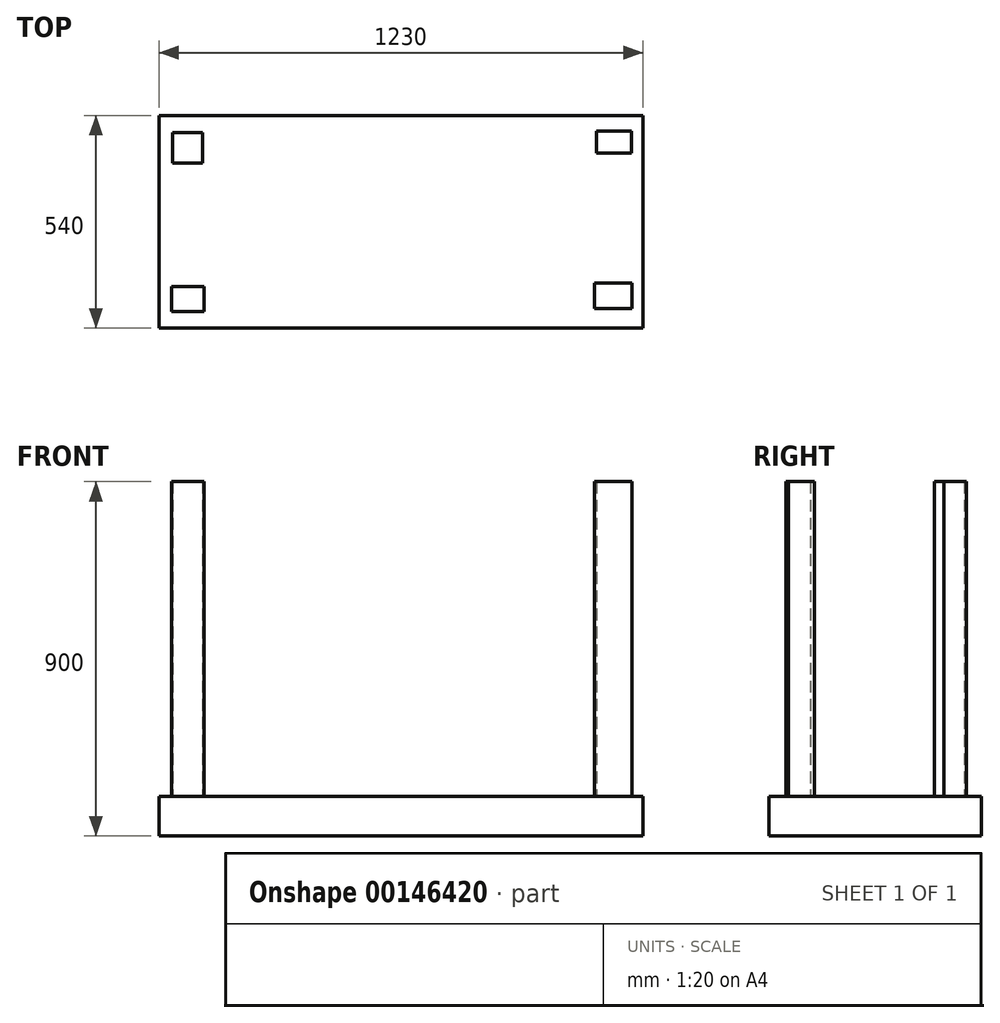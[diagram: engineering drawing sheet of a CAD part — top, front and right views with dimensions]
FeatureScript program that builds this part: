
annotation { "Feature Type Name" : "Feature", "Feature Type Description" : "" }
export const myFeature = defineFeature(function(context is Context, id is Id, definition is map)
    precondition{}
    {
        {
            var Q0;
            Q0=qCreatedBy(makeId("Top.planeOp"),FACE);
            var sketch = newSketch(context, id + "F0", { "sketchPlane" : qUnion([Q0])});
            skLineSegment(sketch, "E0.bottom", {"start": v(615, -270) * mm, "end": v(-615, -270) * mm});
            skLineSegment(sketch, "E0.top", {"start": v(615, 270) * mm, "end": v(-615, 270) * mm});
            skLineSegment(sketch, "E0.left", {"start": v(615, -270) * mm, "end": v(615, 270) * mm});
            skLineSegment(sketch, "E0.right", {"start": v(-615, -270) * mm, "end": v(-615, 270) * mm});
            skPoint(sketch, "E0.middle", {"position": v(0, 0) * mm});
            skSolve(sketch);
        }
        {
            var Q0;
            Q0 = qSketchRegion(id + "F0", true);
            extrude(context, id + "F1", {"entities" : qUnion([Q0]), "depth" : 100 * mm});
        }
        {
            var Q0;
            Q0=makeQuery(id+"F1.opExtrude","CAP_FACE",FACE,{"disambiguationData":[OSD([sQuery(id+"F0.wireOp",EDGE,"E0.bottom"),sQuery(id+"F0.wireOp",EDGE,"E0.top"),sQuery(id+"F0.wireOp",EDGE,"E0.left"),sQuery(id+"F0.wireOp",EDGE,"E0.right")])],"isStart":false});
            var sketch = newSketch(context, id + "F2", { "sketchPlane" : qUnion([Q0])});
            skLineSegment(sketch, "E1.bottom", {"start": v(-582.57, -227.2) * mm, "end": v(-500.5, -227.2) * mm});
            skLineSegment(sketch, "E1.top", {"start": v(-582.57, -164.73) * mm, "end": v(-500.5, -164.73) * mm});
            skLineSegment(sketch, "E1.left", {"start": v(-582.57, -227.2) * mm, "end": v(-582.57, -164.73) * mm});
            skLineSegment(sketch, "E1.right", {"start": v(-500.5, -227.2) * mm, "end": v(-500.5, -164.73) * mm});
            skLineSegment(sketch, "E2.bottom", {"start": v(-580.54, 226.4) * mm, "end": v(-503.8, 226.4) * mm});
            skLineSegment(sketch, "E2.top", {"start": v(-580.54, 150.06) * mm, "end": v(-503.8, 150.06) * mm});
            skLineSegment(sketch, "E2.left", {"start": v(-580.54, 226.4) * mm, "end": v(-580.54, 150.06) * mm});
            skLineSegment(sketch, "E2.right", {"start": v(-503.8, 226.4) * mm, "end": v(-503.8, 150.06) * mm});
            skLineSegment(sketch, "E3.bottom", {"start": v(585.54, 231.05) * mm, "end": v(497.23, 231.05) * mm});
            skLineSegment(sketch, "E3.top", {"start": v(585.54, 175.04) * mm, "end": v(497.23, 175.04) * mm});
            skLineSegment(sketch, "E3.left", {"start": v(585.54, 231.05) * mm, "end": v(585.54, 175.04) * mm});
            skLineSegment(sketch, "E3.right", {"start": v(497.23, 231.05) * mm, "end": v(497.23, 175.04) * mm});
            skLineSegment(sketch, "E4.bottom", {"start": v(587.28, -220.37) * mm, "end": v(491.68, -220.37) * mm});
            skLineSegment(sketch, "E4.top", {"start": v(587.28, -154.91) * mm, "end": v(491.68, -154.91) * mm});
            skLineSegment(sketch, "E4.left", {"start": v(587.28, -220.37) * mm, "end": v(587.28, -154.91) * mm});
            skLineSegment(sketch, "E4.right", {"start": v(491.68, -220.37) * mm, "end": v(491.68, -154.91) * mm});
            skSolve(sketch);
        }
        {
            var Q0;
            Q0=makeQuery(id+"F2.imprint","IMPRINT",FACE,{"disambiguationData":[TD([[makeQuery(id+"F2.imprint","IMPRINT",EDGE,{"derivedFrom":sQuery(id+"F2.wireOp",EDGE,"E2.bottom")}),-1.0]])]});
            var Q1;
            Q1=makeQuery(id+"F2.imprint","IMPRINT",FACE,{"disambiguationData":[TD([[makeQuery(id+"F2.imprint","IMPRINT",EDGE,{"derivedFrom":sQuery(id+"F2.wireOp",EDGE,"E1.bottom")}),1.0]])]});
            var Q2;
            Q2=makeQuery(id+"F2.imprint","IMPRINT",FACE,{"disambiguationData":[TD([[makeQuery(id+"F2.imprint","IMPRINT",EDGE,{"derivedFrom":sQuery(id+"F2.wireOp",EDGE,"E3.bottom")}),1.0]])]});
            var Q3;
            Q3=makeQuery(id+"F2.imprint","IMPRINT",FACE,{"disambiguationData":[TD([[makeQuery(id+"F2.imprint","IMPRINT",EDGE,{"derivedFrom":sQuery(id+"F2.wireOp",EDGE,"E4.bottom")}),-1.0]])]});
            extrude(context, id + "F3", {"entities" : qUnion([Q0, Q1, Q2, Q3]), "operationType" : NewBodyOperationType.ADD, "depth" : 800 * mm});
        }
    });
